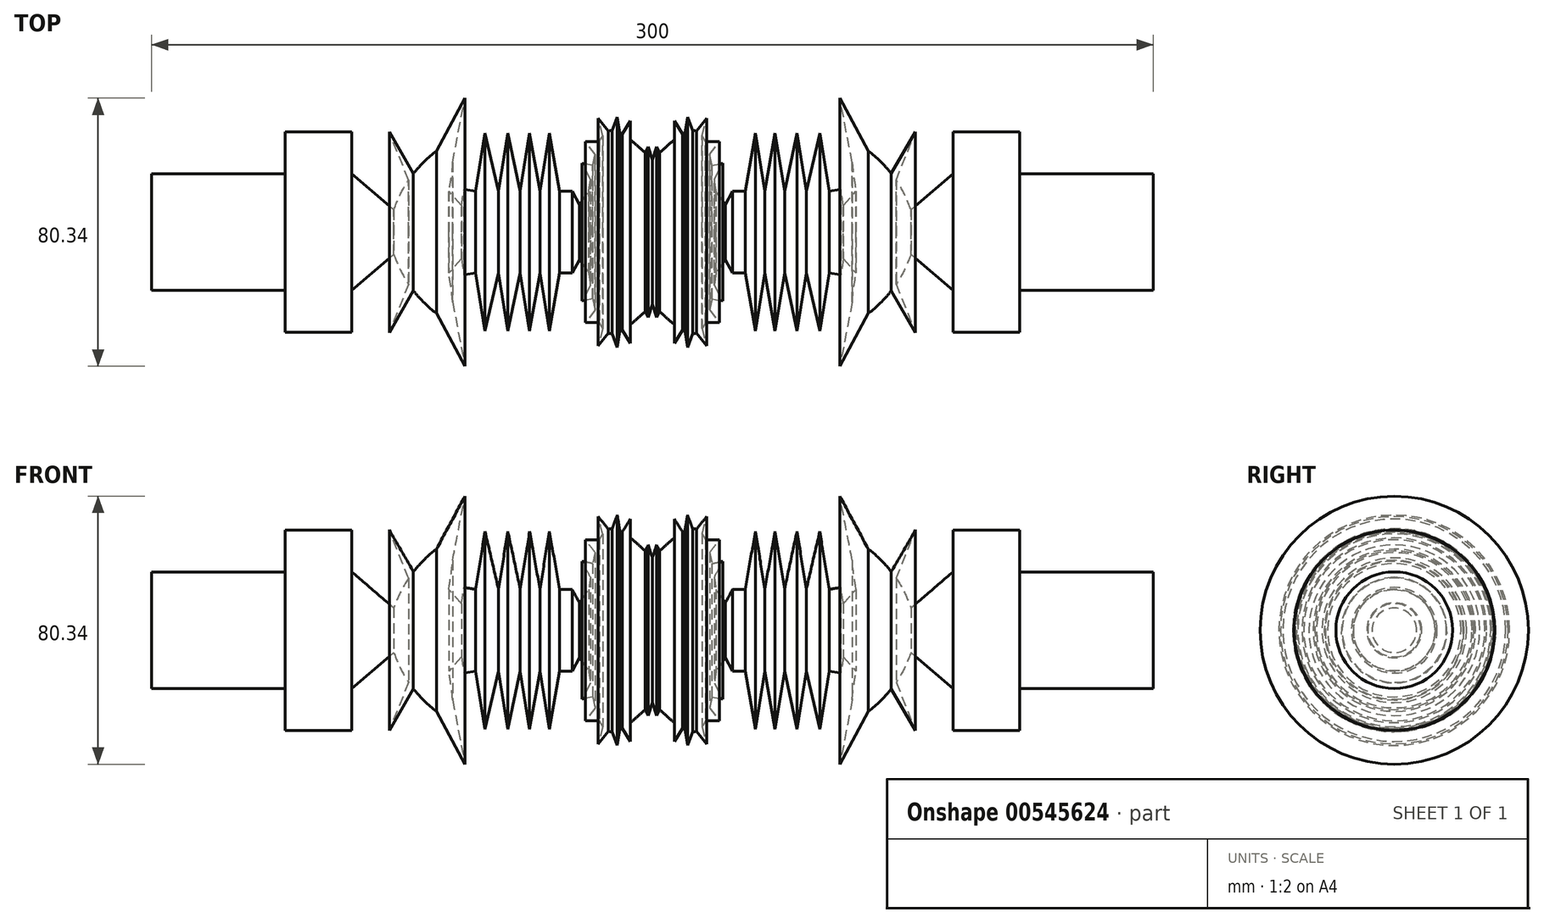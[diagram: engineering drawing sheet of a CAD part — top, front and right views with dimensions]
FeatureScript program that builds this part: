
annotation { "Feature Type Name" : "Feature", "Feature Type Description" : "" }
export const myFeature = defineFeature(function(context is Context, id is Id, definition is map)
    precondition{}
    {
        {
            var Q0;
            Q0=qCreatedBy(makeId("Front.planeOp"),FACE);
            var sketch = newSketch(context, id + "F0", { "sketchPlane" : qUnion([Q0])});
            skLineSegment(sketch, "E0", {"start": v(0, 0) * mm, "end": v(150, 0) * mm});
            skLineSegment(sketch, "E1", {"start": v(150, 0) * mm, "end": v(150, 17.5) * mm});
            skLineSegment(sketch, "E2", {"start": v(150, 17.5) * mm, "end": v(110, 17.5) * mm});
            skLineSegment(sketch, "E3", {"start": v(110, 17.5) * mm, "end": v(110, 30) * mm});
            skLineSegment(sketch, "E4", {"start": v(110, 30) * mm, "end": v(90, 30) * mm});
            skLineSegment(sketch, "E5", {"start": v(90, 30) * mm, "end": v(90, 17.5) * mm});
            skLineSegment(sketch, "E6", {"start": v(0, 21.67) * mm, "end": v(0, 0) * mm});
            skPoint(sketch, "E7.6.internal.orphan", {"position": v(0, 21.67) * mm});
            skFitSpline(sketch, "E8", {"points": [v(0, 21.67) * mm, v(13.16, 30.29) * mm, v(19.06, 12.27) * mm], "startDerivative": vector(31.5, 30.6) * mm, "endDerivative": vector(7, -48.17) * mm});
            skLineSegment(sketch, "E9", {"start": v(19.06, 12.27) * mm, "end": v(21.86, 8.23) * mm});
            skLineSegment(sketch, "E10", {"start": v(21.86, 8.23) * mm, "end": v(24.03, 12.27) * mm});
            skLineSegment(sketch, "E11", {"start": v(24.03, 12.27) * mm, "end": v(27.76, 12.27) * mm});
            skLineSegment(sketch, "E12", {"start": v(27.76, 12.27) * mm, "end": v(30.87, 29.67) * mm});
            skLineSegment(sketch, "E13", {"start": v(30.87, 29.67) * mm, "end": v(33.66, 12.27) * mm});
            skLineSegment(sketch, "E14", {"start": v(33.66, 12.27) * mm, "end": v(36.77, 29.67) * mm});
            skLineSegment(sketch, "E15", {"start": v(36.77, 29.67) * mm, "end": v(39.57, 12.27) * mm});
            skLineSegment(sketch, "E16", {"start": v(39.57, 12.27) * mm, "end": v(43.3, 29.67) * mm});
            skLineSegment(sketch, "E17", {"start": v(43.3, 29.67) * mm, "end": v(46.09, 12.27) * mm});
            skLineSegment(sketch, "E18", {"start": v(46.09, 12.27) * mm, "end": v(50.13, 29.67) * mm});
            skLineSegment(sketch, "E19", {"start": v(50.13, 29.67) * mm, "end": v(52.92, 12.27) * mm});
            skLineSegment(sketch, "E20", {"start": v(52.92, 12.27) * mm, "end": v(56.41, 12.83) * mm});
            skLineSegment(sketch, "E21", {"start": v(56.41, 12.83) * mm, "end": v(57.2, 7.97) * mm});
            skLineSegment(sketch, "E22", {"start": v(57.2, 7.97) * mm, "end": v(61, 12.27) * mm});
            skFitSpline(sketch, "E23", {"points": [v(61, 12.27) * mm, v(61, 25.63) * mm, v(71.56, 17.55) * mm, v(77.47, 6.68) * mm], "startDerivative": vector(-9.27, 55.87) * mm, "endDerivative": vector(12.65, -31.77) * mm});
            skLineSegment(sketch, "E24", {"start": v(77.47, 6.68) * mm, "end": v(90, 17.5) * mm});
            skLineSegment(sketch, "E25", {"start": v(2.21, 23.8) * mm, "end": v(2.21, 30.8) * mm});
            skLineSegment(sketch, "E26", {"start": v(2.21, 30.8) * mm, "end": v(5, 26.53) * mm});
            skLineSegment(sketch, "E27", {"start": v(6.57, 27.68) * mm, "end": v(6.57, 33.34) * mm});
            skLineSegment(sketch, "E28", {"start": v(6.57, 33.34) * mm, "end": v(9.07, 29.4) * mm});
            skLineSegment(sketch, "E29", {"start": v(13.16, 30.29) * mm, "end": v(16.25, 34.07) * mm});
            skLineSegment(sketch, "E30", {"start": v(16.25, 34.07) * mm, "end": v(14.9, 28.88) * mm});
            skLineSegment(sketch, "E31", {"start": v(14.9, 28.88) * mm, "end": v(15.87, 27.14) * mm});
            skLineSegment(sketch, "E32", {"start": v(15.87, 27.14) * mm, "end": v(20.08, 27.14) * mm});
            skLineSegment(sketch, "E33", {"start": v(20.08, 27.14) * mm, "end": v(17.13, 23.28) * mm});
            skLineSegment(sketch, "E34", {"start": v(17.13, 23.28) * mm, "end": v(17.84, 19.97) * mm});
            skLineSegment(sketch, "E35", {"start": v(17.84, 19.97) * mm, "end": v(21.1, 20.67) * mm});
            skLineSegment(sketch, "E36", {"start": v(21.1, 20.67) * mm, "end": v(18.53, 15.89) * mm});
            skLineSegment(sketch, "E37", {"start": v(9.73, 29.76) * mm, "end": v(10.52, 34.54) * mm});
            skLineSegment(sketch, "E38", {"start": v(10.52, 34.54) * mm, "end": v(12.04, 30.44) * mm});
            skLineSegment(sketch, "E39", {"start": v(73, 15.6) * mm, "end": v(78.8, 30.1) * mm});
            skLineSegment(sketch, "E40", {"start": v(78.8, 30.1) * mm, "end": v(71.56, 17.55) * mm});
            skLineSegment(sketch, "E41", {"start": v(61, 25.63) * mm, "end": v(64.66, 24.32) * mm});
            skLineSegment(sketch, "E42", {"start": v(64.66, 24.32) * mm, "end": v(56.15, 40.17) * mm});
            skLineSegment(sketch, "E43", {"start": v(56.15, 40.17) * mm, "end": v(59.83, 20.94) * mm});
            skLineSegment(sketch, "E44", {"start": v(2.21, 23.8) * mm, "end": v(1.23, 25.6) * mm});
            skLineSegment(sketch, "E45", {"start": v(1.23, 25.6) * mm, "end": v(0, 21.67) * mm});
            skSolve(sketch);
        }
        {
            var Q0;
            Q0 = qSketchRegion(id + "F0", true);
            var Q1;
            Q1=sQuery(id+"F0.wireOp",EDGE,"E0");
            revolve(context, id + "F1", {"entities" : qUnion([Q0]), "axis" : qUnion([Q1]), "revolveType" : RevolveType.FULL});
        }
        {
            var Q0;
            Q0=makeQuery(id+"F1.opRevolve","SWEPT_BODY",BODY,{"disambiguationData":[OSD([sQuery(id+"F0.wireOp",EDGE,"E0"),sQuery(id+"F0.wireOp",EDGE,"E1"),sQuery(id+"F0.wireOp",EDGE,"E2"),sQuery(id+"F0.wireOp",EDGE,"E3"),sQuery(id+"F0.wireOp",EDGE,"E4"),sQuery(id+"F0.wireOp",EDGE,"E5"),sQuery(id+"F0.wireOp",EDGE,"E7"),sQuery(id+"F0.wireOp",EDGE,"E6")])]});
            var Q1;
            Q1=makeQuery(id+"F1.opRevolve","SWEPT_FACE",FACE,{"disambiguationData":[OSD([sQuery(id+"F0.wireOp",EDGE,"E6")])]});
            mirror(context, id + "F2", {"operationType" : NewBodyOperationType.ADD, "entities" : qUnion([Q0]), "mirrorPlane" : qUnion([Q1])});
        }
    });
